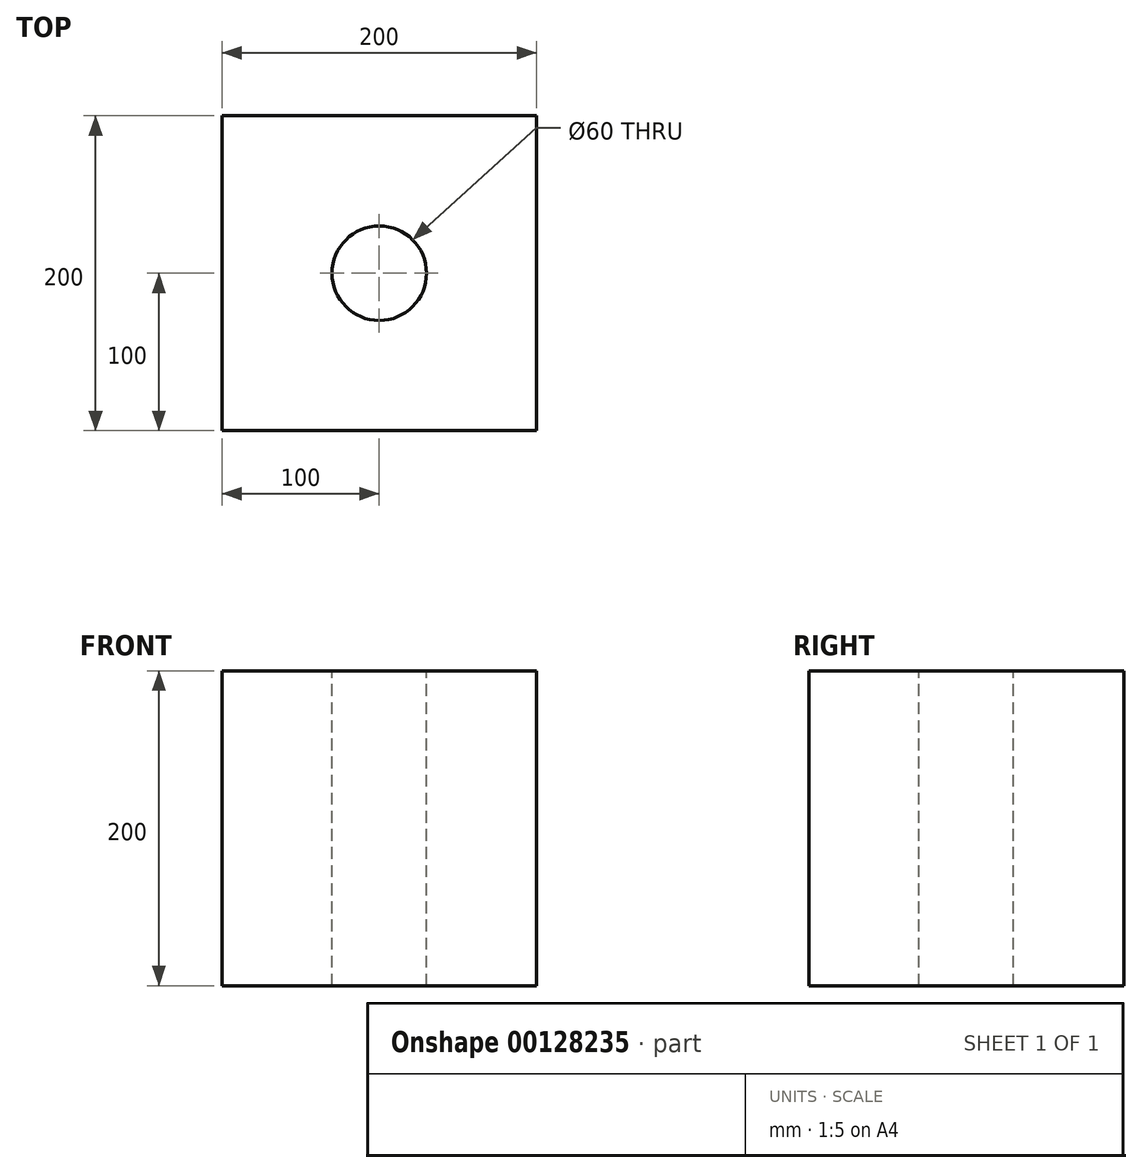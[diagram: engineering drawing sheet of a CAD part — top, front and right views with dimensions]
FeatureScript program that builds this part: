
annotation { "Feature Type Name" : "Feature", "Feature Type Description" : "" }
export const myFeature = defineFeature(function(context is Context, id is Id, definition is map)
    precondition{}
    {
        {
            var Q0;
            Q0=qCreatedBy(makeId("Top.planeOp"),FACE);
            var sketch = newSketch(context, id + "F0", { "sketchPlane" : qUnion([Q0])});
            skLineSegment(sketch, "E0.bottom", {"start": v(100, 100) * mm, "end": v(-100, 100) * mm});
            skLineSegment(sketch, "E0.top", {"start": v(100, -100) * mm, "end": v(-100, -100) * mm});
            skLineSegment(sketch, "E0.left", {"start": v(100, 100) * mm, "end": v(100, -100) * mm});
            skLineSegment(sketch, "E0.right", {"start": v(-100, 100) * mm, "end": v(-100, -100) * mm});
            skPoint(sketch, "E0.middle", {"position": v(0, 0) * mm});
            skSolve(sketch);
        }
        {
            var Q0;
            Q0=makeQuery(id+"F0.imprint","IMPRINT",FACE,{"disambiguationData":[TD([[makeQuery(id+"F0.imprint","IMPRINT",EDGE,{"derivedFrom":sQuery(id+"F0.wireOp",EDGE,"E0.bottom")}),1.0]])]});
            extrude(context, id + "F1", {"entities" : qUnion([Q0]), "depth" : 200 * mm});
        }
        {
            var Q0;
            Q0=makeQuery(id+"F1.opExtrude","CAP_FACE",FACE,{"disambiguationData":[OSD([sQuery(id+"F0.wireOp",EDGE,"E0.bottom"),sQuery(id+"F0.wireOp",EDGE,"E0.top"),sQuery(id+"F0.wireOp",EDGE,"E0.left"),sQuery(id+"F0.wireOp",EDGE,"E0.right")])],"isStart":false});
            var sketch = newSketch(context, id + "F2", { "sketchPlane" : qUnion([Q0])});
            skPoint(sketch, "E1", {"position": v(0, 0) * mm});
            skSolve(sketch);
        }
        {
            var Q0;
            Q0=sQuery(id+"F2.wireOp",VERTEX,"E1");
            var Q1;
            Q1=makeQuery(id+"F1.opExtrude","SWEPT_BODY",BODY,{"disambiguationData":[OSD([sQuery(id+"F0.wireOp",EDGE,"E0.bottom"),sQuery(id+"F0.wireOp",EDGE,"E0.top"),sQuery(id+"F0.wireOp",EDGE,"E0.left"),sQuery(id+"F0.wireOp",EDGE,"E0.right")])]});
            hole(context, id + "F3", {"style" : HoleStyle.SIMPLE, "endStyle" : HoleEndStyle.THROUGH, "holeDiameter" : 60 * mm, "locations" : qUnion([Q0]), "scope" : qUnion([Q1]), "isTappedThrough" : true});
        }
    });
